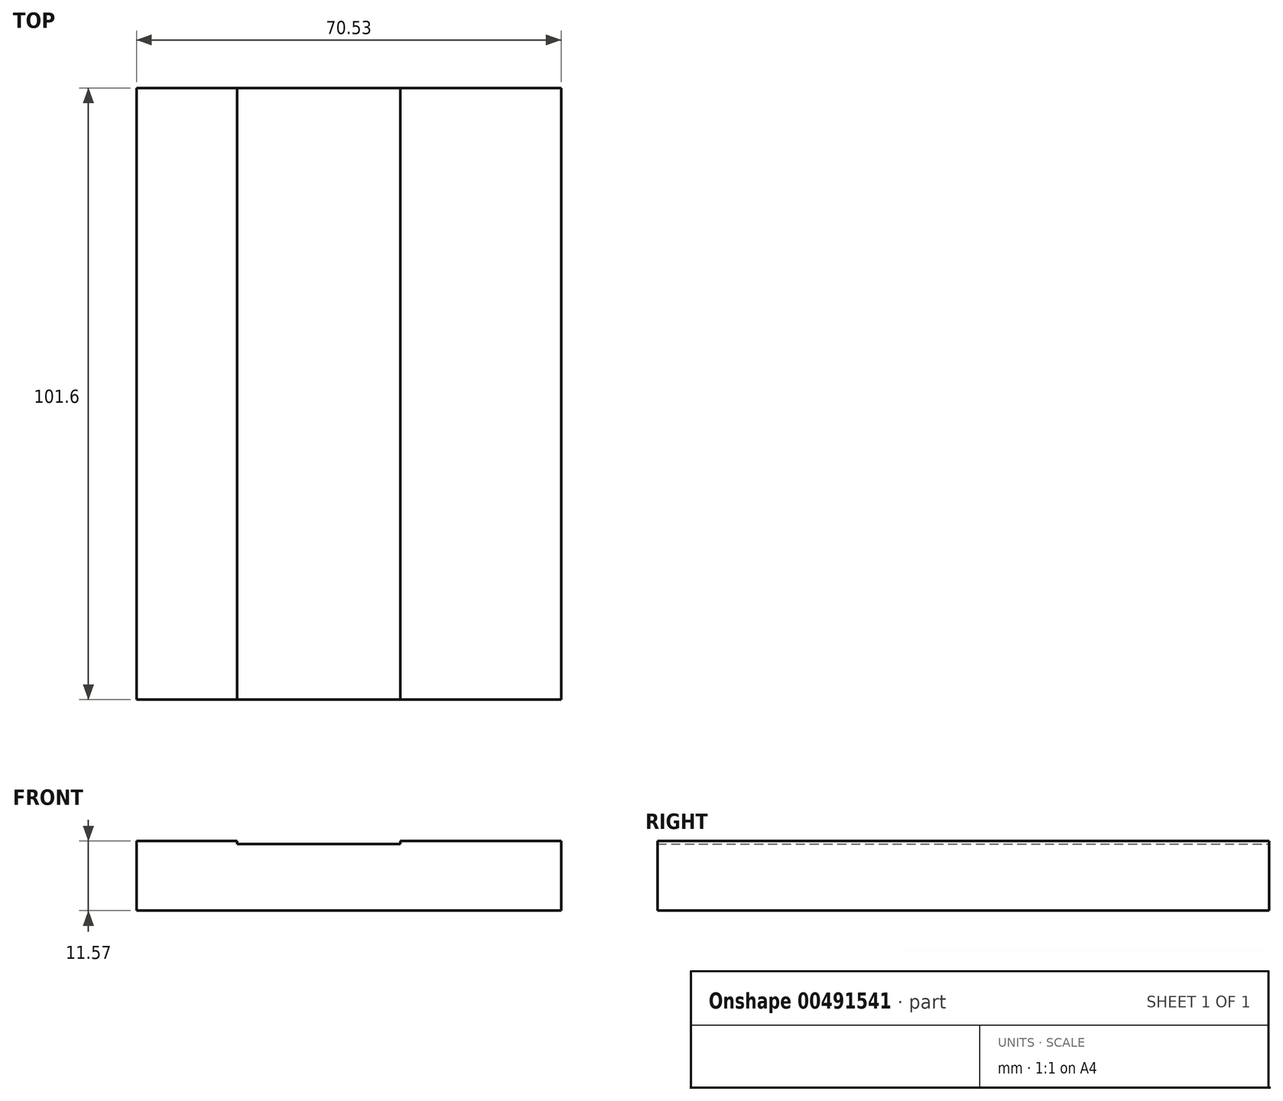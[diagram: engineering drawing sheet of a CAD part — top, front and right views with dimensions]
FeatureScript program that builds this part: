
annotation { "Feature Type Name" : "Feature", "Feature Type Description" : "" }
export const myFeature = defineFeature(function(context is Context, id is Id, definition is map)
    precondition{}
    {
        {
            var Q0;
            Q0=qCreatedBy(makeId("Front.planeOp"),FACE);
            var sketch = newSketch(context, id + "F0", { "sketchPlane" : qUnion([Q0])});
            skLineSegment(sketch, "E0.bottom", {"start": v(0, 0) * mm, "end": v(-70.53, 0) * mm});
            skLineSegment(sketch, "E0.top", {"start": v(0, 11.57) * mm, "end": v(-70.53, 11.57) * mm});
            skLineSegment(sketch, "E0.left", {"start": v(0, 0) * mm, "end": v(0, 11.57) * mm});
            skLineSegment(sketch, "E0.right", {"start": v(-70.53, 0) * mm, "end": v(-70.53, 11.57) * mm});
            skLineSegment(sketch, "E1.bottom", {"start": v(-26.73, 16.4) * mm, "end": v(-53.85, 16.4) * mm});
            skLineSegment(sketch, "E1.top", {"start": v(-26.73, 11.1) * mm, "end": v(-53.85, 11.1) * mm});
            skLineSegment(sketch, "E1.left", {"start": v(-26.73, 16.4) * mm, "end": v(-26.73, 11.1) * mm});
            skLineSegment(sketch, "E1.right", {"start": v(-53.85, 16.4) * mm, "end": v(-53.85, 11.1) * mm});
            skPoint(sketch, "E1.middle", {"position": v(-40.29, 13.75) * mm});
            skSolve(sketch);
        }
        {
            var Q0;
            Q0=makeQuery(id+"F0.imprint","IMPRINT",FACE,{"disambiguationData":[TD([[makeQuery(id+"F0.imprint","IMPRINT",EDGE,{"derivedFrom":sQuery(id+"F0.wireOp",EDGE,"E0.bottom")}),-1.0]])]});
            extrude(context, id + "F1", {"entities" : qUnion([Q0]), "endBound" : BoundingType.SYMMETRIC, "depth" : 101.6 * mm});
        }
    });
